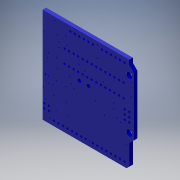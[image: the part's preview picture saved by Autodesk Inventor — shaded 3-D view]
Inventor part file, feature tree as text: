
AUTODESK INVENTOR PART (.ipt)
format: ipt  version: 2016 (Build 200138000, 138)  size: 817,152 bytes
history: native  units: mm
features: other x1, imported_body x1, extrude x1, sketch x1
ambient origin geometry x8: Origin, YZ Plane, XZ Plane, XY Plane, X Axis, Y Axis, Z Axis, Center Point
bodies: Body1 (feature_tree)
feature tree (4):
  other  "Cortar-Extruir2"
  imported_body  "Base1"
  extrude  "Extrusion1"  Depth=10.0mm TaperAngle=0.0deg
  sketch  "Sketch1"  dims[d0=17.5mm d1=10.0mm d2=0.0mm]
